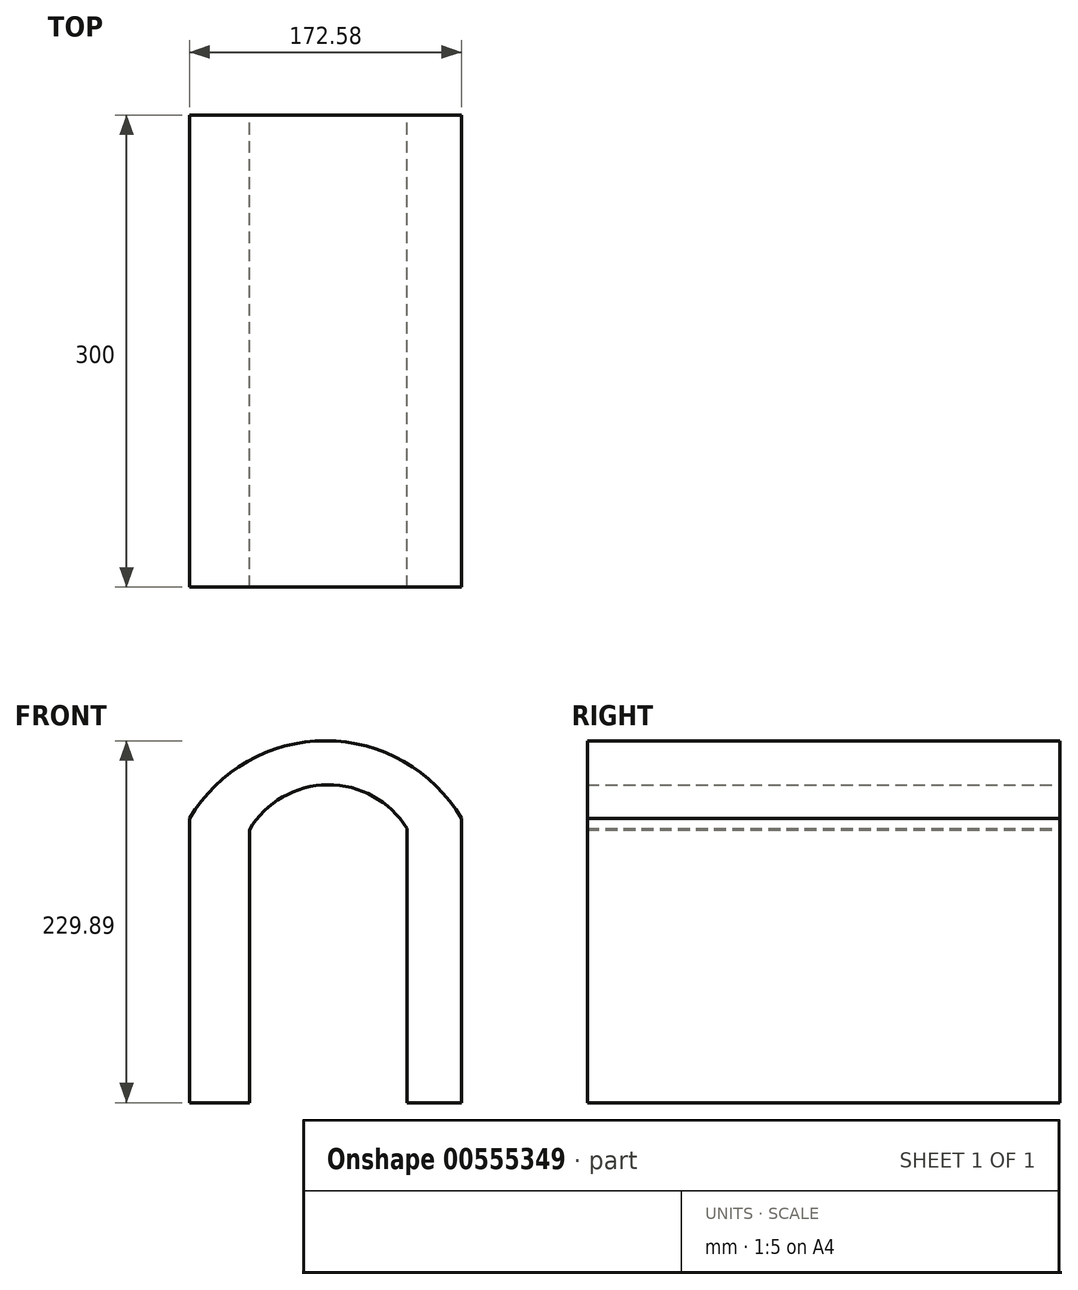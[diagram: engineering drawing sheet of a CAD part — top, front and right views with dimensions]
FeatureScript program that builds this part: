
annotation { "Feature Type Name" : "Feature", "Feature Type Description" : "" }
export const myFeature = defineFeature(function(context is Context, id is Id, definition is map)
    precondition{}
    {
        {
            var Q0;
            Q0=qCreatedBy(makeId("Front.planeOp"),FACE);
            var sketch = newSketch(context, id + "F0", { "sketchPlane" : qUnion([Q0])});
            skLineSegment(sketch, "E0", {"start": v(-172.58, -14.52) * mm, "end": v(-172.58, -195.16) * mm});
            skArc(sketch, "E1", {"start": v(0, -14.52) * mm, "mid": v(-86.3, 34.73) * mm, "end": v(-172.58, -14.52) * mm});
            skLineSegment(sketch, "E2", {"start": v(0, -14.52) * mm, "end": v(0, -195.16) * mm});
            skArc(sketch, "E3", {"start": v(-34.68, -20.97) * mm, "mid": v(-84.9, 6.77) * mm, "end": v(-134.68, -21.77) * mm});
            skLineSegment(sketch, "E4", {"start": v(-134.68, -21.77) * mm, "end": v(-134.68, -195.16) * mm});
            skLineSegment(sketch, "E5", {"start": v(-34.68, -20.97) * mm, "end": v(-34.68, -195.16) * mm});
            skLineSegment(sketch, "E6", {"start": v(-34.68, -195.16) * mm, "end": v(0, -195.16) * mm});
            skLineSegment(sketch, "E7", {"start": v(-172.58, -195.16) * mm, "end": v(-134.68, -195.16) * mm});
            skSolve(sketch);
        }
        {
            var Q0;
            Q0 = qSketchRegion(id + "F0", true);
            var Q1;
            Q1=makeQuery(id+"F0.imprint","IMPRINT",FACE,{"disambiguationData":[TD([[makeQuery(id+"F0.imprint","IMPRINT",EDGE,{"derivedFrom":sQuery(id+"F0.wireOp",EDGE,"E0")}),1.0]])]});
            extrude(context, id + "F1", {"entities" : qUnion([Q0, Q1]), "depth" : 150 * mm, "offsetDistance" : 25 * mm});
        }
        {
            var Q0;
            Q0 = qSketchRegion(id + "F0", true);
            var Q1;
            Q1=makeQuery(id+"F1.opExtrude","CAP_FACE",FACE,{"disambiguationData":[OSD([sQuery(id+"F0.wireOp",EDGE,"E0"),sQuery(id+"F0.wireOp",EDGE,"E1"),sQuery(id+"F0.wireOp",EDGE,"E2"),sQuery(id+"F0.wireOp",EDGE,"E3"),sQuery(id+"F0.wireOp",EDGE,"E4"),sQuery(id+"F0.wireOp",EDGE,"E5"),sQuery(id+"F0.wireOp",EDGE,"E6"),sQuery(id+"F0.wireOp",EDGE,"E7")])],"isStart":true});
            extrude(context, id + "F2", {"entities" : qUnion([Q0, Q1]), "operationType" : NewBodyOperationType.ADD, "oppositeDirection" : true, "depth" : 150 * mm, "offsetDistance" : 25 * mm});
        }
    });
